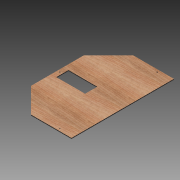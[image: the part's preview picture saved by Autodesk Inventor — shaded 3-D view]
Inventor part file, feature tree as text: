
AUTODESK INVENTOR PART (.ipt)
format: ipt  version: 2015 (Build 190159000, 159)  size: 134,656 bytes
history: native  units: in
note: dims shown in document units (in); Inventor stores cm internally (conversion verified against a paired STEP export)
features: extrude x1, sketch x1
ambient origin geometry x8: Origin, YZ Plane, XZ Plane, XY Plane, X Axis, Y Axis, Z Axis, Center Point
bodies: Body1 (feature_tree)
feature tree (2):
  extrude  "Extrusion5"  Depth=3.0in
  sketch  "Sketch7"  dims[d17=0.2in d18=0.0in d22=3.0in d23=7.1in d24=1.26in d25=0.25in d26=0.63in d27=0.63in d28=6.5in d29=25.26in d31=13.0in d32=10.0in d36=45.0deg d37=8.6691in d38=9.13in]
